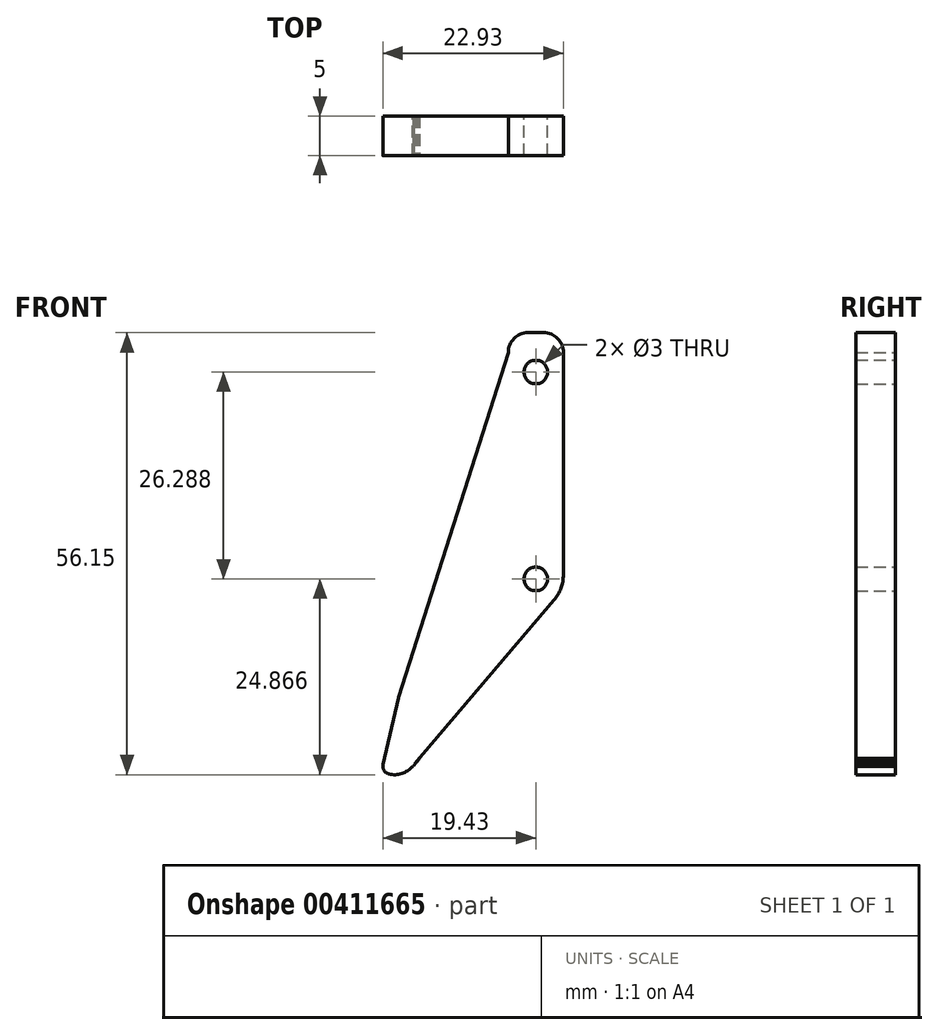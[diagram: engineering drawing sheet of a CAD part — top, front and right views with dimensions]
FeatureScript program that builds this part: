
annotation { "Feature Type Name" : "Feature", "Feature Type Description" : "" }
export const myFeature = defineFeature(function(context is Context, id is Id, definition is map)
    precondition{}
    {
        {
            var Q0;
            Q0=qCreatedBy(makeId("Front.planeOp"),FACE);
            var sketch = newSketch(context, id + "F0", { "sketchPlane" : qUnion([Q0])});
            skLineSegment(sketch, "E0", {"start": v(0, 33.01) * mm, "end": v(0, 7.35) * mm});
            skLineSegment(sketch, "E1", {"start": v(-1.2, 4.11) * mm, "end": v(-13.93, -10.86) * mm});
            skLineSegment(sketch, "E2", {"start": v(-12.49, -19.97) * mm, "end": v(5.8, 1.54) * mm});
            skLineSegment(sketch, "E3", {"start": v(7, 4.78) * mm, "end": v(7, 33.01) * mm});
            skLineSegment(sketch, "E4", {"start": v(4.5, 35.51) * mm, "end": v(2.5, 35.51) * mm});
            skPoint(sketch, "E5.visualSharp", {"position": v(7, 2.94) * mm});
            skArc(sketch, "E5.filletArc", {"start": v(5.8, 1.54) * mm, "mid": v(6.7, 3.05) * mm, "end": v(7, 4.78) * mm});
            skPoint(sketch, "E6.visualSharp", {"position": v(0, 5.51) * mm});
            skArc(sketch, "E6.filletArc", {"start": v(-1.2, 4.11) * mm, "mid": v(-0.3, 5.63) * mm, "end": v(0, 7.35) * mm});
            skCircle(sketch, "E7", {"center": v(3.5, 30.51) * mm, "radius": 1.5 * mm});
            skLineSegment(sketch, "E8", {"start": v(-16.78, -19.6) * mm, "end": v(10.73, 12.72) * mm, "construction": true});
            skLineSegment(sketch, "E9", {"start": v(3.5, 35.51) * mm, "end": v(3.5, -5.59) * mm, "construction": true});
            skCircle(sketch, "E10", {"center": v(-13.54, -15.8) * mm, "radius": 1.5 * mm});
            skPoint(sketch, "E11.visualSharp", {"position": v(-14.1, -21.87) * mm});
            skPoint(sketch, "E12.visualSharp", {"position": v(0, 35.51) * mm});
            skArc(sketch, "E12.filletArc", {"start": v(2.5, 35.51) * mm, "mid": v(0.73, 34.78) * mm, "end": v(0, 33.01) * mm});
            skPoint(sketch, "E13.visualSharp", {"position": v(7, 35.51) * mm});
            skArc(sketch, "E13.filletArc", {"start": v(7, 33.01) * mm, "mid": v(6.27, 34.78) * mm, "end": v(4.5, 35.51) * mm});
            skCircle(sketch, "E14", {"center": v(3.5, 4.23) * mm, "radius": 1.5 * mm});
            skLineSegment(sketch, "E15", {"start": v(-16.08, -20.16) * mm, "end": v(-13.93, -10.86) * mm});
            skLineSegment(sketch, "E16", {"start": v(-12.17, -19.59) * mm, "end": v(-12.49, -19.97) * mm});
            skArc(sketch, "E17.filletArc", {"start": v(-16.08, -20.16) * mm, "mid": v(-14.02, -20.61) * mm, "end": v(-12.17, -19.59) * mm});
            skLineSegment(sketch, "E18", {"start": v(-13.93, -10.86) * mm, "end": v(0, 33.01) * mm});
            skSolve(sketch);
        }
        {
            var Q0;
            Q0 = qSketchRegion(id + "F0", true);
            extrude(context, id + "F1", {"entities" : qUnion([Q0]), "depth" : 5 * mm});
        }
        {
            var Q0;
            Q0=makeQuery(id+"F1.opExtrude","SWEPT_EDGE",EDGE,{"disambiguationData":[OSD([sQuery(id+"F0.wireOp",EDGE,"E15"),sQuery(id+"F0.wireOp",EDGE,"E17.filletArc")])]});
            fillet(context, id + "F2", {"entities" : qUnion([Q0]), "radius" : 1 * mm, "tangentPropagation" : true, "allowEdgeOverflow" : false});
        }
        {
            var Q0;
            Q0=makeQuery(id+"F1.opExtrude","SWEPT_EDGE",EDGE,{"disambiguationData":[OSD([sQuery(id+"F0.wireOp",EDGE,"E1"),sQuery(id+"F0.wireOp",EDGE,"E15")])]});
            fillet(context, id + "F3", {"entities" : qUnion([Q0]), "radius" : 1 * mm, "tangentPropagation" : true, "allowEdgeOverflow" : false});
        }
        {
            var Q0;
            Q0=makeQuery(id+"F1.opExtrude","CAP_FACE",FACE,{"disambiguationData":[OSD([sQuery(id+"F0.wireOp",EDGE,"E2"),sQuery(id+"F0.wireOp",EDGE,"E3"),sQuery(id+"F0.wireOp",EDGE,"E4"),sQuery(id+"F0.wireOp",EDGE,"E5.filletArc"),sQuery(id+"F0.wireOp",EDGE,"E7"),sQuery(id+"F0.wireOp",EDGE,"E12.filletArc"),sQuery(id+"F0.wireOp",EDGE,"E13.filletArc"),sQuery(id+"F0.wireOp",EDGE,"E14"),sQuery(id+"F0.wireOp",EDGE,"E15"),sQuery(id+"F0.wireOp",EDGE,"E17.filletArc"),sQuery(id+"F0.wireOp",EDGE,"E18")])],"isStart":false});
            var sketch = newSketch(context, id + "F4", { "sketchPlane" : qUnion([Q0])});
            skLineSegment(sketch, "E19", {"start": v(-12.17, -19.59) * mm, "end": v(-12.08, -19.49) * mm});
            skLineSegment(sketch, "E20", {"start": v(-12.08, -19.49) * mm, "end": v(-12.04, -19.61) * mm});
            skLineSegment(sketch, "E21", {"start": v(-12.04, -19.61) * mm, "end": v(-12.17, -19.59) * mm});
            skLineSegment(sketch, "E22.1.0.0", {"start": v(-11.95, -19.51) * mm, "end": v(-12.08, -19.49) * mm});
            skLineSegment(sketch, "E22.1.0.1", {"start": v(-12, -19.39) * mm, "end": v(-11.95, -19.51) * mm});
            skLineSegment(sketch, "E22.1.0.2", {"start": v(-12.08, -19.49) * mm, "end": v(-12, -19.39) * mm});
            skLineSegment(sketch, "E22.2.0.0", {"start": v(-11.87, -19.41) * mm, "end": v(-12, -19.39) * mm});
            skLineSegment(sketch, "E22.2.0.1", {"start": v(-11.91, -19.29) * mm, "end": v(-11.87, -19.41) * mm});
            skLineSegment(sketch, "E22.2.0.2", {"start": v(-12, -19.39) * mm, "end": v(-11.91, -19.29) * mm});
            skLineSegment(sketch, "E22.3.0.0", {"start": v(-11.78, -19.31) * mm, "end": v(-11.91, -19.29) * mm});
            skLineSegment(sketch, "E22.3.0.1", {"start": v(-11.83, -19.19) * mm, "end": v(-11.78, -19.31) * mm});
            skLineSegment(sketch, "E22.3.0.2", {"start": v(-11.91, -19.29) * mm, "end": v(-11.83, -19.19) * mm});
            skLineSegment(sketch, "E22.4.0.0", {"start": v(-11.7, -19.21) * mm, "end": v(-11.83, -19.19) * mm});
            skLineSegment(sketch, "E22.4.0.1", {"start": v(-11.74, -19.09) * mm, "end": v(-11.7, -19.21) * mm});
            skLineSegment(sketch, "E22.4.0.2", {"start": v(-11.83, -19.19) * mm, "end": v(-11.74, -19.09) * mm});
            skLineSegment(sketch, "E22.5.0.0", {"start": v(-11.61, -19.11) * mm, "end": v(-11.74, -19.09) * mm});
            skLineSegment(sketch, "E22.5.0.1", {"start": v(-11.66, -19) * mm, "end": v(-11.61, -19.11) * mm});
            skLineSegment(sketch, "E22.5.0.2", {"start": v(-11.74, -19.09) * mm, "end": v(-11.66, -19) * mm});
            skLineSegment(sketch, "E22.6.0.0", {"start": v(-11.53, -19.01) * mm, "end": v(-11.66, -19) * mm});
            skLineSegment(sketch, "E22.6.0.1", {"start": v(-11.57, -18.9) * mm, "end": v(-11.53, -19.01) * mm});
            skLineSegment(sketch, "E22.6.0.2", {"start": v(-11.66, -19) * mm, "end": v(-11.57, -18.9) * mm});
            skLineSegment(sketch, "E22.7.0.0", {"start": v(-11.44, -18.91) * mm, "end": v(-11.57, -18.9) * mm});
            skLineSegment(sketch, "E22.7.0.1", {"start": v(-11.49, -18.8) * mm, "end": v(-11.44, -18.91) * mm});
            skLineSegment(sketch, "E22.7.0.2", {"start": v(-11.57, -18.9) * mm, "end": v(-11.49, -18.8) * mm});
            skLineSegment(sketch, "E22.8.0.0", {"start": v(-11.36, -18.82) * mm, "end": v(-11.49, -18.8) * mm});
            skLineSegment(sketch, "E22.8.0.1", {"start": v(-11.4, -18.7) * mm, "end": v(-11.36, -18.82) * mm});
            skLineSegment(sketch, "E22.8.0.2", {"start": v(-11.49, -18.8) * mm, "end": v(-11.4, -18.7) * mm});
            skLineSegment(sketch, "E22.9.0.0", {"start": v(-11.28, -18.72) * mm, "end": v(-11.4, -18.7) * mm});
            skLineSegment(sketch, "E22.9.0.1", {"start": v(-11.32, -18.6) * mm, "end": v(-11.28, -18.72) * mm});
            skLineSegment(sketch, "E22.9.0.2", {"start": v(-11.4, -18.7) * mm, "end": v(-11.32, -18.6) * mm});
            skLineSegment(sketch, "E22.direction1", {"start": v(-12.17, -19.59) * mm, "end": v(-12.08, -19.49) * mm, "construction": true});
            skSolve(sketch);
        }
        {
            var Q0;
            Q0 = qSketchRegion(id + "F4", true);
            var Q1;
            {var subQ5=sQuery(id+"F4.wireOp",EDGE,"E22.3.0.2");var subQ6=sQuery(id+"F4.wireOp",EDGE,"E22.2.0.1");var subQ7=makeQuery(id+"F4.imprint","INTERSECT",VERTEX,{"derivedFrom":[subQ6,subQ5]});Q1=makeQuery(id+"F4.imprint","IMPRINT",FACE,{"disambiguationData":[TD([[makeQuery(id+"F4.imprint","IMPRINT",EDGE,{"disambiguationData":[TD([[subQ7,-1.0]])],"derivedFrom":subQ6}),1.0]])]});}
            extrude(context, id + "F5", {"entities" : qUnion([Q0, Q1]), "operationType" : NewBodyOperationType.ADD, "oppositeDirection" : true, "depth" : 5 * mm});
        }
    });
